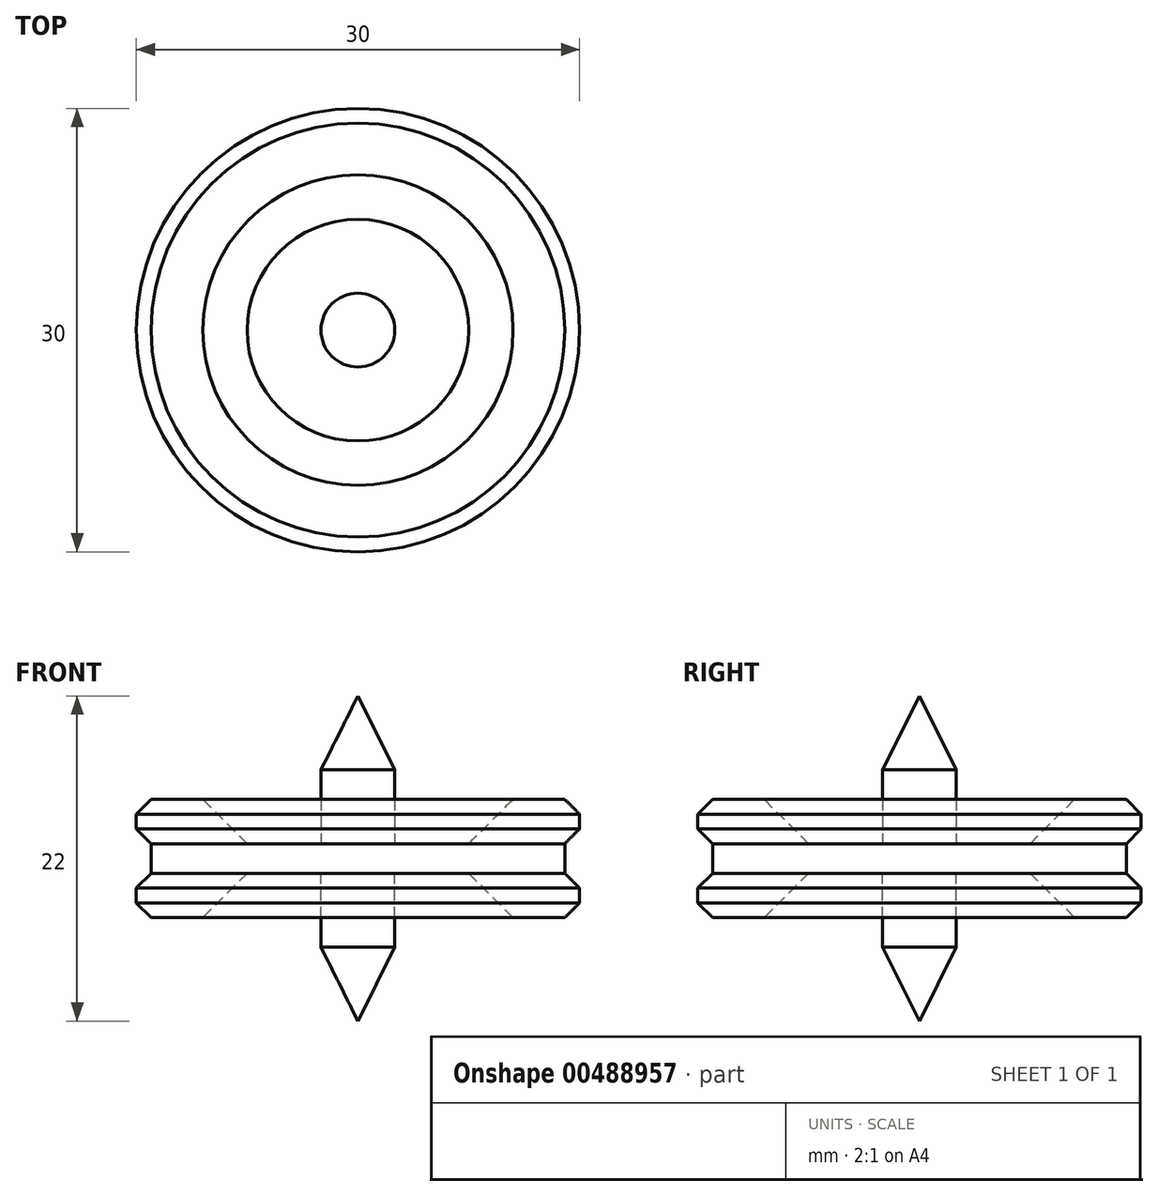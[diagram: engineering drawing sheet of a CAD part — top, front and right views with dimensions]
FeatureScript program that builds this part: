
annotation { "Feature Type Name" : "Feature", "Feature Type Description" : "" }
export const myFeature = defineFeature(function(context is Context, id is Id, definition is map)
    precondition{}
    {
        {
            var Q0;
            Q0=qCreatedBy(makeId("Top.planeOp"),FACE);
            var sketch = newSketch(context, id + "F0", { "sketchPlane" : qUnion([Q0])});
            skCircle(sketch, "E0", {"center": v(0, 0) * mm, "radius": 14 * mm});
            skSolve(sketch);
        }
        {
            var Q0;
            Q0=makeQuery(id+"F0.imprint","IMPRINT",FACE,{"disambiguationData":[TD([[makeQuery(id+"F0.imprint","IMPRINT",EDGE,{"derivedFrom":sQuery(id+"F0.wireOp",EDGE,"E0")}),1.0]])]});
            extrude(context, id + "F1", {"entities" : qUnion([Q0]), "depth" : 1 * mm});
        }
        {
            var Q0;
            Q0=makeQuery(id+"F1.opExtrude","CAP_FACE",FACE,{"disambiguationData":[OSD([sQuery(id+"F0.wireOp",EDGE,"E0")])],"isStart":false});
            var sketch = newSketch(context, id + "F2", { "sketchPlane" : qUnion([Q0])});
            skCircle(sketch, "E1", {"center": v(0, 0) * mm, "radius": 15 * mm});
            skCircle(sketch, "E2", {"center": v(0, 0) * mm, "radius": 7.5 * mm});
            skCircle(sketch, "E3", {"center": v(0, 0) * mm, "radius": 2.5 * mm});
            skSolve(sketch);
        }
        {
            var Q0;
            Q0=makeQuery(id+"F2.imprint","IMPRINT",FACE,{"disambiguationData":[TD([[makeQuery(id+"F2.imprint","IMPRINT",EDGE,{"derivedFrom":sQuery(id+"F2.wireOp",EDGE,"E1")}),1.0]])]});
            var Q1;
            Q1=makeQuery(id+"F2.imprint","IMPRINT",FACE,{"disambiguationData":[TD([[makeQuery(id+"F2.imprint","IMPRINT",EDGE,{"derivedFrom":sQuery(id+"F2.wireOp",EDGE,"E2")}),-1.0]])]});
            extrude(context, id + "F3", {"entities" : qUnion([Q0, Q1]), "operationType" : NewBodyOperationType.ADD, "depth" : 3 * mm});
        }
        {
            var Q0;
            Q0=makeQuery(id+"F2.imprint","IMPRINT",FACE,{"disambiguationData":[TD([[makeQuery(id+"F2.imprint","IMPRINT",EDGE,{"derivedFrom":sQuery(id+"F2.wireOp",EDGE,"E3")}),1.0]])]});
            extrude(context, id + "F4", {"entities" : qUnion([Q0]), "operationType" : NewBodyOperationType.ADD, "depth" : 10 * mm});
        }
        {
            var Q0;
            Q0=makeQuery(id+"F3.opExtrude","CAP_EDGE",EDGE,{"disambiguationData":[OSD([sQuery(id+"F2.wireOp",EDGE,"E1")])],"isStart":false});
            var Q1;
            Q1=makeQuery(id+"F3.opExtrude","CAP_EDGE",EDGE,{"disambiguationData":[OSD([sQuery(id+"F2.wireOp",EDGE,"E1")])],"isStart":true});
            chamfer(context, id + "F5", {"entities" : qUnion([Q0, Q1]), "width" : 1 * mm, "tangentPropagation" : true});
        }
        {
            var Q0;
            Q0=makeQuery(id+"F3.opExtrude","CAP_EDGE",EDGE,{"disambiguationData":[OSD([sQuery(id+"F2.wireOp",EDGE,"E2")])],"isStart":false});
            chamfer(context, id + "F6", {"entities" : qUnion([Q0]), "width" : 3 * mm, "tangentPropagation" : true});
        }
        {
            var Q0;
            Q0=makeQuery(id+"F4.opExtrude","CAP_EDGE",EDGE,{"disambiguationData":[OSD([sQuery(id+"F2.wireOp",EDGE,"E3")])],"isStart":false});
            chamfer(context, id + "F7", {"entities" : qUnion([Q0]), "chamferType" : ChamferType.TWO_OFFSETS, "width1" : 2.5 * mm, "oppositeDirection" : false, "width2" : 5 * mm, "tangentPropagation" : true});
        }
        {
            var Q0;
            Q0=makeQuery(id+"F1.opExtrude","SWEPT_BODY",BODY,{"disambiguationData":[OSD([sQuery(id+"F0.wireOp",EDGE,"E0")])]});
            var Q1;
            Q1=qCreatedBy(makeId("Top.planeOp"),FACE);
            mirror(context, id + "F8", {"operationType" : NewBodyOperationType.ADD, "entities" : qUnion([Q0]), "mirrorPlane" : qUnion([Q1])});
        }
    });
